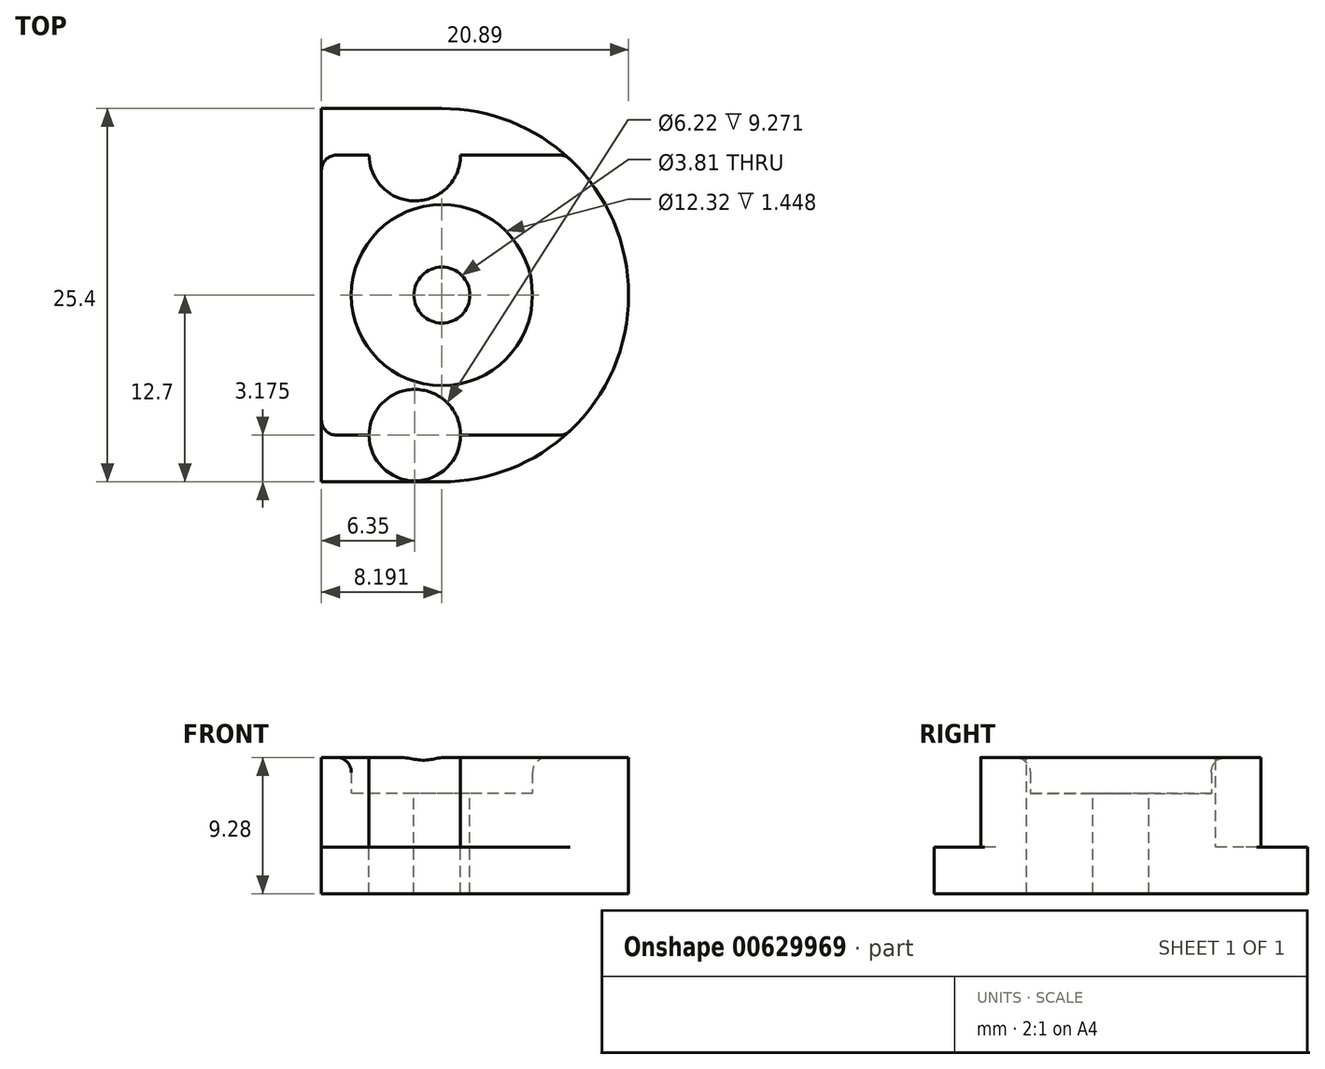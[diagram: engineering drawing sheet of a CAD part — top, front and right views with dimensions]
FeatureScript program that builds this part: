
annotation { "Feature Type Name" : "Feature", "Feature Type Description" : "" }
export const myFeature = defineFeature(function(context is Context, id is Id, definition is map)
    precondition{}
    {
        {
            var Q0;
            Q0=qCreatedBy(makeId("Top.planeOp"),FACE);
            var sketch = newSketch(context, id + "F0", { "sketchPlane" : qUnion([Q0])});
            skLineSegment(sketch, "E0.bottom", {"start": v(1.84, 12.7) * mm, "end": v(-6.35, 12.7) * mm});
            skLineSegment(sketch, "E0.top", {"start": v(1.84, -12.7) * mm, "end": v(-6.35, -12.7) * mm});
            skLineSegment(sketch, "E0.left", {"start": v(6.35, 12.7) * mm, "end": v(6.35, 11.87) * mm});
            skLineSegment(sketch, "E0.right", {"start": v(-6.35, 12.7) * mm, "end": v(-6.35, -12.7) * mm});
            skPoint(sketch, "E0.middle", {"position": v(0, 0) * mm});
            skCircle(sketch, "E1", {"center": v(1.84, 0) * mm, "radius": 6.16 * mm});
            skCircle(sketch, "E2", {"center": v(1.84, 0) * mm, "radius": 1.9 * mm});
            skLineSegment(sketch, "E3.MirrorCS", {"start": v(-19.05, 12.7) * mm, "end": v(-19.05, -12.7) * mm});
            skLineSegment(sketch, "E4.MirrorCS", {"start": v(-19.05, 12.7) * mm, "end": v(-6.35, 12.7) * mm});
            skLineSegment(sketch, "E5.MirrorCS", {"start": v(-19.05, -12.7) * mm, "end": v(-6.35, -12.7) * mm});
            skLineSegment(sketch, "E6", {"start": v(-12.7, 12.7) * mm, "end": v(-12.7, -12.7) * mm, "construction": true});
            skCircle(sketch, "E7", {"center": v(-12.7, 9.53) * mm, "radius": 1.84 * mm});
            skLineSegment(sketch, "E8", {"start": v(-14.54, 9.53) * mm, "end": v(-14.54, 12.7) * mm});
            skLineSegment(sketch, "E9", {"start": v(-10.86, 9.53) * mm, "end": v(-10.86, 12.7) * mm});
            skCircle(sketch, "E10.MirrorC", {"center": v(-12.7, -9.53) * mm, "radius": 1.84 * mm});
            skLineSegment(sketch, "E11.MirrorCS", {"start": v(-14.54, -9.53) * mm, "end": v(-14.54, -12.7) * mm});
            skLineSegment(sketch, "E12.MirrorCS", {"start": v(-10.86, -9.53) * mm, "end": v(-10.86, -12.7) * mm});
            skArc(sketch, "E13", {"start": v(1.84, -12.7) * mm, "mid": v(14.54, 0) * mm, "end": v(1.84, 12.7) * mm});
            skLineSegment(sketch, "E14.bottom", {"start": v(1.84, 12.7) * mm, "end": v(-1.33, 12.7) * mm});
            skLineSegment(sketch, "E14.top", {"start": v(1.84, -12.7) * mm, "end": v(-1.27, -12.7) * mm});
            skPoint(sketch, "E15.orphan", {"position": v(12.7, -12.7) * mm});
            skLineSegment(sketch, "E16.trimOffspring", {"start": v(6.35, -11.87) * mm, "end": v(6.35, -12.7) * mm});
            skPoint(sketch, "E17.center.orphan", {"position": v(1.84, 9.9) * mm});
            skPoint(sketch, "E17.end.orphan", {"position": v(5.08, 9.9) * mm});
            skPoint(sketch, "E17.start.orphan", {"position": v(-1.27, 9.9) * mm});
            skPoint(sketch, "E18.MirrorCS.end.orphan", {"position": v(5.08, -9.9) * mm});
            skPoint(sketch, "E18.MirrorCS.start.orphan", {"position": v(-1.27, -9.9) * mm});
            skPoint(sketch, "E19.orphan", {"position": v(5.02, -12.7) * mm});
            skPoint(sketch, "E14.left.start.orphan", {"position": v(4.95, 12.7) * mm});
            skCircle(sketch, "E20", {"center": v(0, 9.53) * mm, "radius": 3.11 * mm});
            skLineSegment(sketch, "E21", {"start": v(3.11, 9.53) * mm, "end": v(10.24, 9.53) * mm});
            skLineSegment(sketch, "E22", {"start": v(-3.11, 9.53) * mm, "end": v(-6.35, 9.53) * mm});
            skCircle(sketch, "E23.MirrorC", {"center": v(0, -9.53) * mm, "radius": 3.11 * mm});
            skLineSegment(sketch, "E24.MirrorCS", {"start": v(3.11, -9.53) * mm, "end": v(10.24, -9.53) * mm});
            skLineSegment(sketch, "E25.MirrorCS", {"start": v(-3.11, -9.53) * mm, "end": v(-6.35, -9.53) * mm});
            skSolve(sketch);
        }
        {
            var Q0;
            {var subQ5=sQuery(id+"F0.wireOp",EDGE,"E3.MirrorCS");Q0=makeQuery(id+"F0.imprint","IMPRINT",FACE,{"disambiguationData":[TD([[makeQuery(id+"F0.imprint","IMPRINT",EDGE,{"derivedFrom":subQ5}),1.0]])]});}
            var Q1;
            {var subQ2=sQuery(id+"F0.wireOp",EDGE,"E21");Q1=makeQuery(id+"F0.imprint","IMPRINT",FACE,{"disambiguationData":[TD([[makeQuery(id+"F0.imprint","IMPRINT",EDGE,{"derivedFrom":subQ2}),1.0]])]});}
            var Q2;
            {var subQ7=sQuery(id+"F0.wireOp",EDGE,"9953c4cf-a746-45d5-82f6-0a46f51aa50a.trimOffspring");Q2=makeQuery(id+"F0.imprint","IMPRINT",FACE,{"disambiguationData":[TD([[makeQuery(id+"F0.imprint","IMPRINT",EDGE,{"derivedFrom":subQ7}),-1.0]])]});}
            var Q3;
            {var subQ4=sQuery(id+"F0.wireOp",EDGE,"9953c4cf-a746-45d5-82f6-0a46f51aa50a.trimOffspring");Q3=makeQuery(id+"F0.imprint","IMPRINT",FACE,{"disambiguationData":[TD([[makeQuery(id+"F0.imprint","IMPRINT",EDGE,{"derivedFrom":subQ4}),1.0]])]});}
            var Q4;
            {var subQ2=sQuery(id+"F0.wireOp",EDGE,"E17");Q4=makeQuery(id+"F0.imprint","IMPRINT",FACE,{"disambiguationData":[TD([[makeQuery(id+"F0.imprint","IMPRINT",EDGE,{"derivedFrom":subQ2}),-1.0]])]});}
            var Q5;
            {var subQ4=sQuery(id+"F0.wireOp",EDGE,"aWKY10aT-Vrg7-qgci-qj0N-tPX5nb9idn5U");Q5=makeQuery(id+"F0.imprint","IMPRINT",FACE,{"disambiguationData":[TD([[makeQuery(id+"F0.imprint","IMPRINT",EDGE,{"derivedFrom":subQ4}),1.0]])]});}
            var Q6;
            {var subQ0=sQuery(id+"F0.wireOp",EDGE,"E17");Q6=makeQuery(id+"F0.imprint","IMPRINT",FACE,{"disambiguationData":[TD([[makeQuery(id+"F0.imprint","IMPRINT",EDGE,{"derivedFrom":subQ0}),1.0]])]});}
            var Q7;
            {var subQ3=sQuery(id+"F0.wireOp",EDGE,"E18.MirrorCS");Q7=makeQuery(id+"F0.imprint","IMPRINT",FACE,{"disambiguationData":[TD([[makeQuery(id+"F0.imprint","IMPRINT",EDGE,{"derivedFrom":subQ3}),-1.0]])]});}
            var Q8;
            {var subQ6=sQuery(id+"F0.wireOp",EDGE,"E18.MirrorCS");Q8=makeQuery(id+"F0.imprint","IMPRINT",FACE,{"disambiguationData":[TD([[makeQuery(id+"F0.imprint","IMPRINT",EDGE,{"derivedFrom":subQ6}),1.0]])]});}
            var Q9;
            {var subQ0=sQuery(id+"F0.wireOp",EDGE,"E14.right");var subQ1=sQuery(id+"F0.wireOp",EDGE,"E13");var subQ2=makeQuery(id+"F0.imprint","INTERSECT",VERTEX,{"disambiguationData":[OD(1.0)],"derivedFrom":[subQ1,subQ0]});Q9=makeQuery(id+"F0.imprint","IMPRINT",FACE,{"disambiguationData":[TD([[makeQuery(id+"F0.imprint","IMPRINT",EDGE,{"disambiguationData":[TD([[subQ2,1.0]])],"derivedFrom":subQ1}),-1.0]])]});}
            var Q10;
            {var subQ0=sQuery(id+"F0.wireOp",EDGE,"E14.right");var subQ1=sQuery(id+"F0.wireOp",EDGE,"E13");var subQ2=makeQuery(id+"F0.imprint","INTERSECT",VERTEX,{"disambiguationData":[OD(0.0)],"derivedFrom":[subQ1,subQ0]});Q10=makeQuery(id+"F0.imprint","IMPRINT",FACE,{"disambiguationData":[TD([[makeQuery(id+"F0.imprint","IMPRINT",EDGE,{"disambiguationData":[TD([[subQ2,-1.0]])],"derivedFrom":subQ1}),-1.0]])]});}
            var Q11;
            Q11=makeQuery(id+"F0.imprint","IMPRINT",FACE,{"disambiguationData":[TD([[makeQuery(id+"F0.imprint","IMPRINT",EDGE,{"derivedFrom":sQuery(id+"F0.wireOp",EDGE,"E1")}),-1.0]])]});
            var Q12;
            {var subQ0=sQuery(id+"F0.wireOp",EDGE,"E20");var subQ1=makeQuery(id+"F0.imprint","INTERSECT",VERTEX,{"derivedFrom":[subQ0,sQuery(id+"F0.wireOp",EDGE,"E21")]});Q12=makeQuery(id+"F0.imprint","IMPRINT",FACE,{"disambiguationData":[TD([[makeQuery(id+"F0.imprint","IMPRINT",EDGE,{"disambiguationData":[TD([[subQ1,-1.0]])],"derivedFrom":subQ0}),1.0]])]});}
            var Q13;
            Q13=makeQuery(id+"F0.imprint","IMPRINT",FACE,{"disambiguationData":[TD([[makeQuery(id+"F0.imprint","IMPRINT",EDGE,{"derivedFrom":sQuery(id+"F0.wireOp",EDGE,"E1")}),1.0]])]});
            var Q14;
            {var subQ0=sQuery(id+"F0.wireOp",EDGE,"E23.MirrorC");var subQ1=makeQuery(id+"F0.imprint","INTERSECT",VERTEX,{"derivedFrom":[subQ0,sQuery(id+"F0.wireOp",EDGE,"E24.MirrorCS")]});Q14=makeQuery(id+"F0.imprint","IMPRINT",FACE,{"disambiguationData":[TD([[makeQuery(id+"F0.imprint","IMPRINT",EDGE,{"disambiguationData":[TD([[subQ1,-1.0]])],"derivedFrom":subQ0}),-1.0]])]});}
            var Q15;
            {var subQ8=sQuery(id+"F0.wireOp",EDGE,"E24.MirrorCS");Q15=makeQuery(id+"F0.imprint","IMPRINT",FACE,{"disambiguationData":[TD([[makeQuery(id+"F0.imprint","IMPRINT",EDGE,{"derivedFrom":subQ8}),-1.0]])]});}
            extrude(context, id + "F1", {"entities" : qUnion([Q0, Q1, Q2, Q3, Q4, Q5, Q6, Q7, Q8, Q9, Q10, Q11, Q12, Q13, Q14, Q15]), "oppositeDirection" : true, "depth" : 3.17 * mm, "offsetDistance" : 25.4 * mm});
        }
        {
            var Q0;
            {var subQ4=sQuery(id+"F0.wireOp",EDGE,"aWKY10aT-Vrg7-qgci-qj0N-tPX5nb9idn5U");Q0=makeQuery(id+"F0.imprint","IMPRINT",FACE,{"disambiguationData":[TD([[makeQuery(id+"F0.imprint","IMPRINT",EDGE,{"derivedFrom":subQ4}),1.0]])]});}
            var Q1;
            {var subQ4=sQuery(id+"F0.wireOp",EDGE,"9953c4cf-a746-45d5-82f6-0a46f51aa50a.trimOffspring");Q1=makeQuery(id+"F0.imprint","IMPRINT",FACE,{"disambiguationData":[TD([[makeQuery(id+"F0.imprint","IMPRINT",EDGE,{"derivedFrom":subQ4}),1.0]])]});}
            var Q2;
            {var subQ7=sQuery(id+"F0.wireOp",EDGE,"9953c4cf-a746-45d5-82f6-0a46f51aa50a.trimOffspring");Q2=makeQuery(id+"F0.imprint","IMPRINT",FACE,{"disambiguationData":[TD([[makeQuery(id+"F0.imprint","IMPRINT",EDGE,{"derivedFrom":subQ7}),-1.0]])]});}
            var Q3;
            {var subQ2=sQuery(id+"F0.wireOp",EDGE,"E17");Q3=makeQuery(id+"F0.imprint","IMPRINT",FACE,{"disambiguationData":[TD([[makeQuery(id+"F0.imprint","IMPRINT",EDGE,{"derivedFrom":subQ2}),-1.0]])]});}
            var Q4;
            {var subQ6=sQuery(id+"F0.wireOp",EDGE,"E18.MirrorCS");Q4=makeQuery(id+"F0.imprint","IMPRINT",FACE,{"disambiguationData":[TD([[makeQuery(id+"F0.imprint","IMPRINT",EDGE,{"derivedFrom":subQ6}),1.0]])]});}
            var Q5;
            Q5=makeQuery(id+"F0.imprint","IMPRINT",FACE,{"disambiguationData":[TD([[makeQuery(id+"F0.imprint","IMPRINT",EDGE,{"derivedFrom":sQuery(id+"F0.wireOp",EDGE,"E1")}),-1.0]])]});
            extrude(context, id + "F2", {"entities" : qUnion([Q0, Q1, Q2, Q3, Q4, Q5]), "operationType" : NewBodyOperationType.ADD, "depth" : 6.1 * mm, "offsetDistance" : 25.4 * mm});
        }
        {
            var Q0;
            Q0=makeQuery(id+"F0.imprint","IMPRINT",FACE,{"disambiguationData":[TD([[makeQuery(id+"F0.imprint","IMPRINT",EDGE,{"derivedFrom":sQuery(id+"F0.wireOp",EDGE,"E1")}),1.0]])]});
            var Q1;
            Q1=makeQuery(id+"F0.imprint","IMPRINT",FACE,{"disambiguationData":[TD([[makeQuery(id+"F0.imprint","IMPRINT",EDGE,{"derivedFrom":sQuery(id+"F0.wireOp",EDGE,"E1")}),1.0]])]});
            var Q2;
            Q2=makeQuery(id+"F0.imprint","IMPRINT",FACE,{"disambiguationData":[TD([[makeQuery(id+"F0.imprint","IMPRINT",EDGE,{"derivedFrom":sQuery(id+"F0.wireOp",EDGE,"E1")}),1.0]])]});
            var Q3;
            Q3=makeQuery(id+"F1.opExtrude","CAP_FACE",FACE,{"disambiguationData":[OSD([sQuery(id+"F0.wireOp",EDGE,"E0.bottom"),sQuery(id+"F0.wireOp",EDGE,"E0.top"),sQuery(id+"F0.wireOp",EDGE,"E2"),sQuery(id+"F0.wireOp",EDGE,"E3.MirrorCS"),sQuery(id+"F0.wireOp",EDGE,"E4.MirrorCS"),sQuery(id+"F0.wireOp",EDGE,"E5.MirrorCS"),sQuery(id+"F0.wireOp",EDGE,"E7"),sQuery(id+"F0.wireOp",EDGE,"E8"),sQuery(id+"F0.wireOp",EDGE,"E9"),sQuery(id+"F0.wireOp",EDGE,"E10.MirrorC"),sQuery(id+"F0.wireOp",EDGE,"E11.MirrorCS"),sQuery(id+"F0.wireOp",EDGE,"E12.MirrorCS"),sQuery(id+"F0.wireOp",EDGE,"E13")])],"isStart":false});
            extrude(context, id + "F3", {"entities" : qUnion([Q0, Q1, Q2]), "operationType" : NewBodyOperationType.ADD, "depth" : 3.63 * mm, "offsetDistance" : 25.4 * mm, "hasSecondDirection" : true, "secondDirectionBound" : BoundingType.UP_TO_SURFACE, "secondDirectionOppositeDirection" : true, "secondDirectionDepth" : 25.4 * mm, "secondDirectionBoundEntityFace" : qUnion([Q3])});
        }
        {
            var Q0;
            Q0=makeQuery(id+"F2.opExtrude","SWEPT_EDGE",EDGE,{"disambiguationData":[OSD([sQuery(id+"F0.wireOp",EDGE,"E0.right"),sQuery(id+"F0.wireOp",EDGE,"E22")])]});
            var Q1;
            Q1=makeQuery(id+"F2.opExtrude","SWEPT_EDGE",EDGE,{"disambiguationData":[OSD([sQuery(id+"F0.wireOp",EDGE,"E0.right"),sQuery(id+"F0.wireOp",EDGE,"E25.MirrorCS")])]});
            var Q2;
            Q2=makeQuery(id+"F2.opExtrude","CAP_EDGE",EDGE,{"disambiguationData":[OSD([sQuery(id+"F0.wireOp",EDGE,"E1")])],"isStart":false});
            var Q3;
            Q3=makeQuery(id+"F2.opExtrude","SWEPT_EDGE",EDGE,{"disambiguationData":[OSD([sQuery(id+"F0.wireOp",EDGE,"E13"),sQuery(id+"F0.wireOp",EDGE,"E21")])]});
            var Q4;
            Q4=makeQuery(id+"F2.opExtrude","SWEPT_EDGE",EDGE,{"disambiguationData":[OSD([sQuery(id+"F0.wireOp",EDGE,"E13"),sQuery(id+"F0.wireOp",EDGE,"E24.MirrorCS")])]});
            var Q5;
            Q5=makeQuery(id+"F2.opExtrude","CAP_EDGE",EDGE,{"disambiguationData":[OSD([sQuery(id+"F0.wireOp",EDGE,"E21")])],"isStart":true});
            var Q6;
            Q6=makeQuery(id+"F2.opExtrude","CAP_EDGE",EDGE,{"disambiguationData":[OSD([sQuery(id+"F0.wireOp",EDGE,"E24.MirrorCS")])],"isStart":true});
            var Q7;
            Q7=makeQuery(id+"F2.opExtrude","CAP_EDGE",EDGE,{"disambiguationData":[OSD([sQuery(id+"F0.wireOp",EDGE,"E23.MirrorC")])],"isStart":true});
            var Q8;
            Q8=makeQuery(id+"F2.opExtrude","CAP_EDGE",EDGE,{"disambiguationData":[OSD([sQuery(id+"F0.wireOp",EDGE,"E20")])],"isStart":true});
            fillet(context, id + "F4", {"entities" : qUnion([Q0, Q1, Q2, Q3, Q4, Q5, Q6, Q7, Q8]), "radius" : 1.02 * mm, "tangentPropagation" : true, "allowEdgeOverflow" : false});
        }
    });
